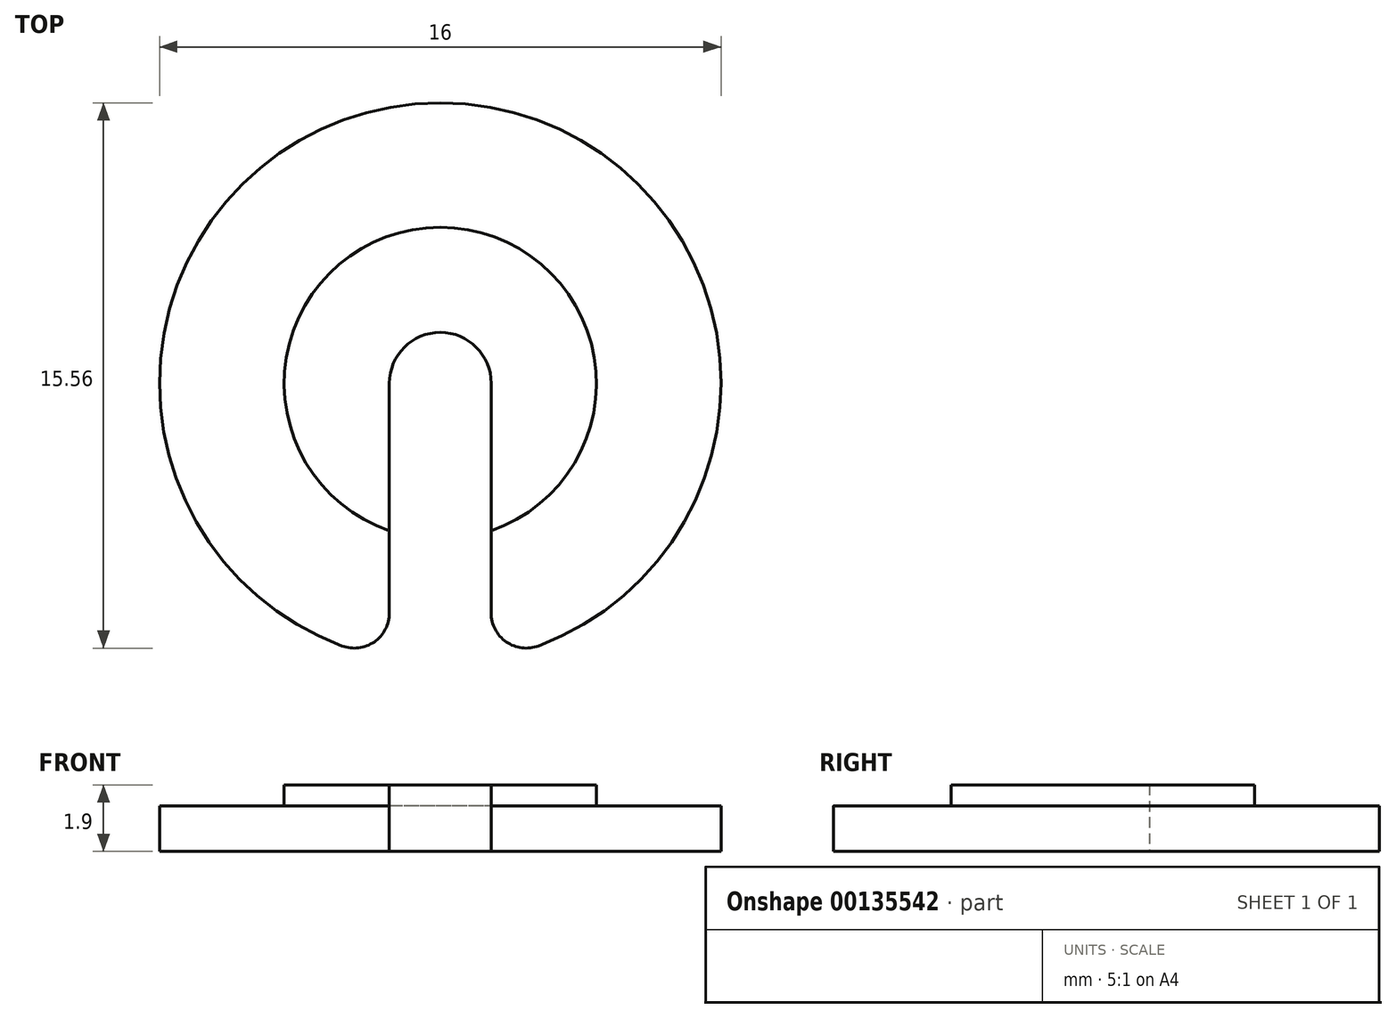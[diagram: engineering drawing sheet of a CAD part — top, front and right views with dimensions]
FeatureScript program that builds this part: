
annotation { "Feature Type Name" : "Feature", "Feature Type Description" : "" }
export const myFeature = defineFeature(function(context is Context, id is Id, definition is map)
    precondition{}
    {
        {
            var Q0;
            Q0=qCreatedBy(makeId("Top.planeOp"),FACE);
            var sketch = newSketch(context, id + "F0", { "sketchPlane" : qUnion([Q0])});
            skArc(sketch, "E0", {"start": v(1.45, 0) * mm, "mid": v(0, 1.45) * mm, "end": v(-1.45, 0) * mm});
            skArc(sketch, "E1", {"start": v(2.8, -7.5) * mm, "mid": v(0, 8) * mm, "end": v(-2.8, -7.5) * mm});
            skLineSegment(sketch, "E2", {"start": v(-1.45, 0) * mm, "end": v(-1.45, -6.56) * mm});
            skLineSegment(sketch, "E3", {"start": v(1.45, -6.56) * mm, "end": v(1.45, 0) * mm});
            skPoint(sketch, "E4.visualSharp", {"position": v(-1.45, -7.87) * mm});
            skArc(sketch, "E4.filletArc", {"start": v(-2.8, -7.5) * mm, "mid": v(-1.88, -7.38) * mm, "end": v(-1.45, -6.56) * mm});
            skPoint(sketch, "E5.visualSharp", {"position": v(1.45, -7.87) * mm});
            skArc(sketch, "E5.filletArc", {"start": v(1.45, -6.56) * mm, "mid": v(1.88, -7.38) * mm, "end": v(2.8, -7.5) * mm});
            skSolve(sketch);
        }
        {
            var Q0;
            Q0 = qSketchRegion(id + "F0", true);
            extrude(context, id + "F1", {"entities" : qUnion([Q0]), "depth" : 1.9 * mm});
        }
        {
            var Q0;
            Q0=makeQuery(id+"F1.opExtrude","CAP_FACE",FACE,{"disambiguationData":[OSD([sQuery(id+"F0.wireOp",EDGE,"E0"),sQuery(id+"F0.wireOp",EDGE,"E1"),sQuery(id+"F0.wireOp",EDGE,"E2"),sQuery(id+"F0.wireOp",EDGE,"E3"),sQuery(id+"F0.wireOp",EDGE,"E4.filletArc"),sQuery(id+"F0.wireOp",EDGE,"E5.filletArc")])],"isStart":false});
            var sketch = newSketch(context, id + "F2", { "sketchPlane" : qUnion([Q0])});
            skCircle(sketch, "E6", {"center": v(0, 0) * mm, "radius": 4.45 * mm});
            skCircle(sketch, "E7", {"center": v(0, 0) * mm, "radius": 8 * mm});
            skSolve(sketch);
        }
        {
            var Q0;
            Q0 = qSketchRegion(id + "F2", true);
            extrude(context, id + "F3", {"entities" : qUnion([Q0]), "operationType" : NewBodyOperationType.REMOVE, "oppositeDirection" : true, "depth" : 0.6 * mm});
        }
    });
